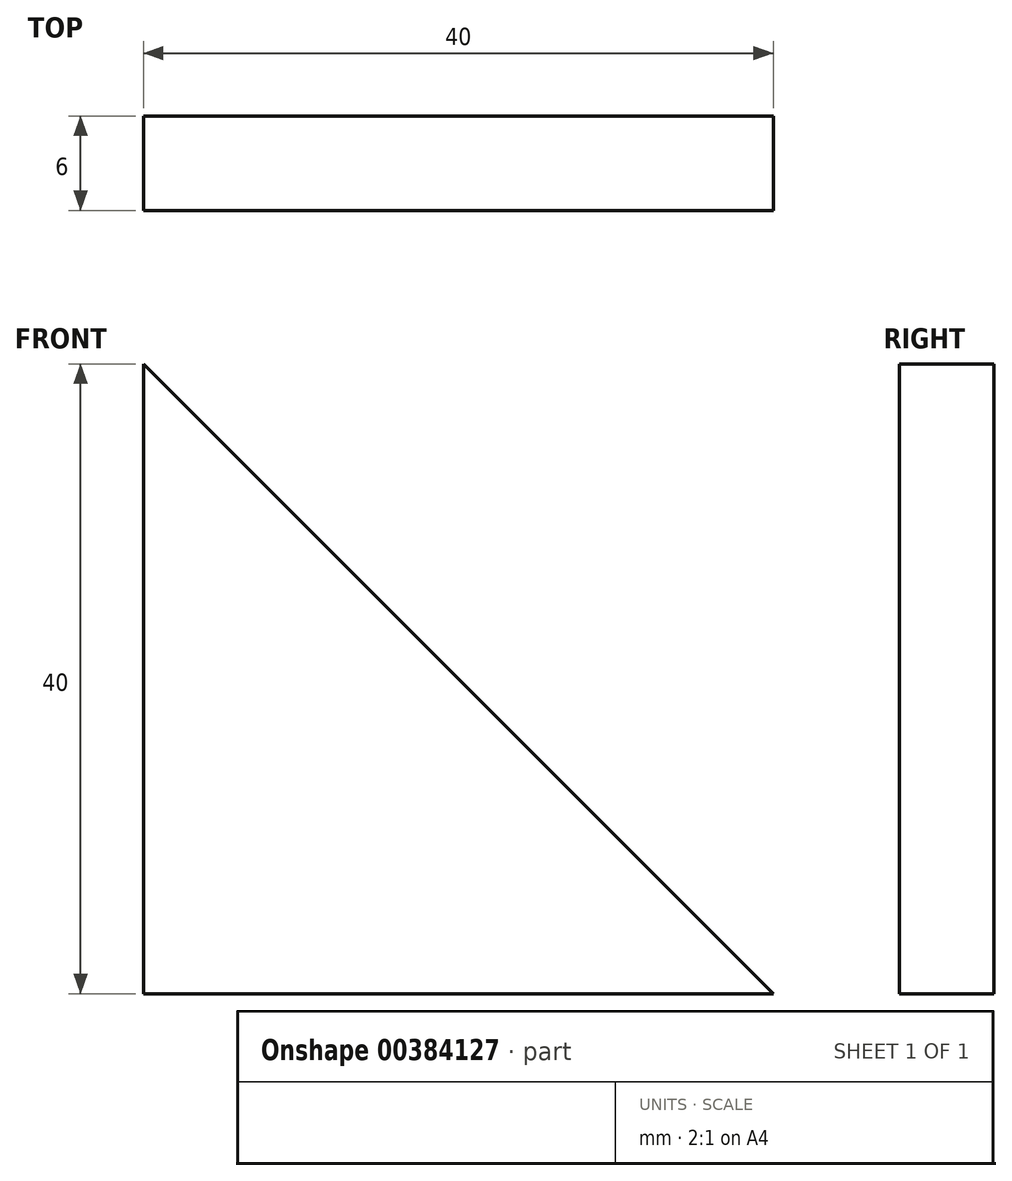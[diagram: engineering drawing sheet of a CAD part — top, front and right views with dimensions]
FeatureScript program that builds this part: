
annotation { "Feature Type Name" : "Feature", "Feature Type Description" : "" }
export const myFeature = defineFeature(function(context is Context, id is Id, definition is map)
    precondition{}
    {
        {
            var Q0;
            Q0=qCreatedBy(makeId("Front.planeOp"),FACE);
            var sketch = newSketch(context, id + "F0", { "sketchPlane" : qUnion([Q0])});
            skLineSegment(sketch, "E0.bottom", {"start": v(0, 0) * mm, "end": v(40, 0) * mm});
            skLineSegment(sketch, "E0.left", {"start": v(0, 0) * mm, "end": v(0, 40) * mm});
            skLineSegment(sketch, "E1", {"start": v(0, 40) * mm, "end": v(40, 0) * mm});
            skSolve(sketch);
        }
        {
            var Q0;
            Q0=qSketchRegion(id+"F0",true);
            var Q1;
            Q1=makeQuery(id+"F0.imprint","IMPRINT",FACE,{"disambiguationData":[TD([[makeQuery(id+"F0.imprint","IMPRINT",EDGE,{"derivedFrom":sQuery(id+"F0.wireOp",EDGE,"E0.bottom")}),1.0]])]});
            extrude(context, id + "F1", {"entities" : qUnion([Q0, Q1]), "depth" : 6 * mm});
        }
    });
